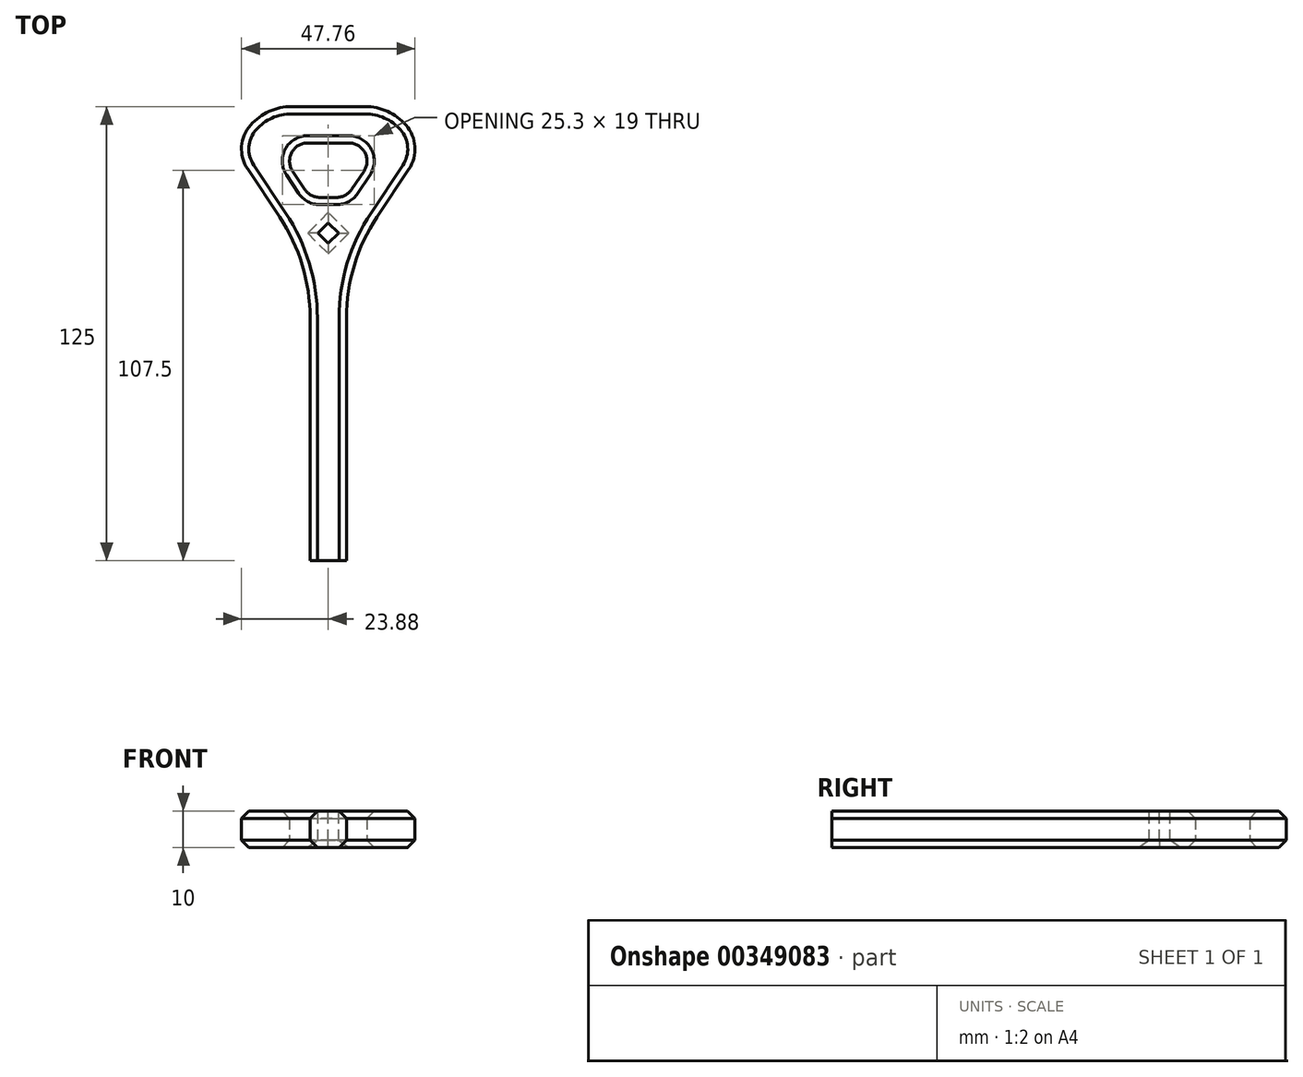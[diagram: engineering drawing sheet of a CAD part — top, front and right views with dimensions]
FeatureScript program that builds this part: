
annotation { "Feature Type Name" : "Feature", "Feature Type Description" : "" }
export const myFeature = defineFeature(function(context is Context, id is Id, definition is map)
    precondition{}
    {
        {
            var Q0;
            Q0=qCreatedBy(makeId("Top.planeOp"),FACE);
            var sketch = newSketch(context, id + "F0", { "sketchPlane" : qUnion([Q0])});
            skLineSegment(sketch, "E0.bottom", {"start": v(-5, 50) * mm, "end": v(5, 50) * mm});
            skLineSegment(sketch, "E0.top", {"start": v(-5, -50) * mm, "end": v(5, -50) * mm});
            skLineSegment(sketch, "E0.left", {"start": v(-5, 31.97) * mm, "end": v(-5, -50) * mm});
            skLineSegment(sketch, "E0.right", {"start": v(5, 31.97) * mm, "end": v(5, -50) * mm});
            skPoint(sketch, "E0.middle", {"position": v(0, 0) * mm});
            skLineSegment(sketch, "E1.bottom", {"start": v(-15, 75) * mm, "end": v(15, 75) * mm});
            skLineSegment(sketch, "E1.top", {"start": v(-15, 65) * mm, "end": v(15, 65) * mm});
            skLineSegment(sketch, "E1.left", {"start": v(-15, 75) * mm, "end": v(-15, 65) * mm});
            skLineSegment(sketch, "E1.right", {"start": v(15, 75) * mm, "end": v(15, 65) * mm});
            skPoint(sketch, "E1.middle", {"position": v(0, 70) * mm});
            skLineSegment(sketch, "E2", {"start": v(-15, 65) * mm, "end": v(-5, 50) * mm});
            skLineSegment(sketch, "E3", {"start": v(5, 50) * mm, "end": v(15, 65) * mm});
            skLineSegment(sketch, "E4", {"start": v(-5, 31.97) * mm, "end": v(-25, 61.97) * mm});
            skLineSegment(sketch, "E5", {"start": v(-25, 61.97) * mm, "end": v(-25, 75) * mm});
            skLineSegment(sketch, "E6", {"start": v(-25, 75) * mm, "end": v(-15, 75) * mm});
            skLineSegment(sketch, "E7.MirrorCS", {"start": v(5, 31.97) * mm, "end": v(25, 61.97) * mm});
            skLineSegment(sketch, "E8.MirrorCS", {"start": v(25, 75) * mm, "end": v(15, 75) * mm});
            skLineSegment(sketch, "E9.MirrorCS", {"start": v(25, 61.97) * mm, "end": v(25, 75) * mm});
            skSolve(sketch);
        }
        {
            var Q0;
            Q0=makeQuery(id+"F0.imprint","IMPRINT",FACE,{"disambiguationData":[TD([[makeQuery(id+"F0.imprint","IMPRINT",EDGE,{"derivedFrom":sQuery(id+"F0.wireOp",EDGE,"E0.bottom")}),-1.0]])]});
            var Q1;
            Q1=makeQuery(id+"F0.imprint","IMPRINT",FACE,{"disambiguationData":[TD([[makeQuery(id+"F0.imprint","IMPRINT",EDGE,{"derivedFrom":sQuery(id+"F0.wireOp",EDGE,"E1.bottom")}),-1.0]])]});
            extrude(context, id + "F1", {"entities" : qUnion([Q0, Q1]), "depth" : 10 * mm});
        }
        {
            var Q0;
            Q0=makeQuery(id+"F1.opExtrude","SWEPT_EDGE",EDGE,{"disambiguationData":[OSD([sQuery(id+"F0.wireOp",EDGE,"E1.top"),sQuery(id+"F0.wireOp",EDGE,"E1.right"),sQuery(id+"F0.wireOp",EDGE,"E3")])]});
            var Q1;
            Q1=makeQuery(id+"F1.opExtrude","SWEPT_EDGE",EDGE,{"disambiguationData":[OSD([sQuery(id+"F0.wireOp",EDGE,"E1.top"),sQuery(id+"F0.wireOp",EDGE,"E1.left"),sQuery(id+"F0.wireOp",EDGE,"E2")])]});
            var Q2;
            Q2=makeQuery(id+"F1.opExtrude","SWEPT_EDGE",EDGE,{"disambiguationData":[OSD([sQuery(id+"F0.wireOp",EDGE,"E0.bottom"),sQuery(id+"F0.wireOp",EDGE,"E2")])]});
            var Q3;
            Q3=makeQuery(id+"F1.opExtrude","SWEPT_EDGE",EDGE,{"disambiguationData":[OSD([sQuery(id+"F0.wireOp",EDGE,"E0.bottom"),sQuery(id+"F0.wireOp",EDGE,"E3")])]});
            fillet(context, id + "F2", {"entities" : qUnion([Q0, Q1, Q2, Q3]), "radius" : 5 * mm, "tangentPropagation" : true, "allowEdgeOverflow" : false});
        }
        {
            var Q0;
            Q0=makeQuery(id+"F1.opExtrude","SWEPT_EDGE",EDGE,{"disambiguationData":[OSD([sQuery(id+"F0.wireOp",EDGE,"E5"),sQuery(id+"F0.wireOp",EDGE,"E6")])]});
            var Q1;
            Q1=makeQuery(id+"F1.opExtrude","SWEPT_EDGE",EDGE,{"disambiguationData":[OSD([sQuery(id+"F0.wireOp",EDGE,"E8.MirrorCS"),sQuery(id+"F0.wireOp",EDGE,"E9.MirrorCS")])]});
            fillet(context, id + "F3", {"entities" : qUnion([Q0, Q1]), "radius" : 15 * mm, "tangentPropagation" : true, "allowEdgeOverflow" : false});
        }
        {
            var Q0;
            Q0=makeQuery(id+"F3.opFillet","BLEND_EDGE",EDGE,{"blendedFrom":[makeQuery(id+"F1.opExtrude","SWEPT_EDGE",EDGE,{"disambiguationData":[OSD([sQuery(id+"F0.wireOp",EDGE,"E5"),sQuery(id+"F0.wireOp",EDGE,"E6")])]}),makeQuery(id+"F1.opExtrude","SWEPT_FACE",FACE,{"disambiguationData":[OSD([sQuery(id+"F0.wireOp",EDGE,"E4")])]})],"blendedInto":[makeQuery(id+"F1.opExtrude","SWEPT_FACE",FACE,{"disambiguationData":[OSD([sQuery(id+"F0.wireOp",EDGE,"E4")])]})]});
            var Q1;
            Q1=makeQuery(id+"F3.opFillet","BLEND_EDGE",EDGE,{"blendedFrom":[makeQuery(id+"F1.opExtrude","SWEPT_EDGE",EDGE,{"disambiguationData":[OSD([sQuery(id+"F0.wireOp",EDGE,"E8.MirrorCS"),sQuery(id+"F0.wireOp",EDGE,"E9.MirrorCS")])]}),makeQuery(id+"F1.opExtrude","SWEPT_FACE",FACE,{"disambiguationData":[OSD([sQuery(id+"F0.wireOp",EDGE,"E7.MirrorCS")])]})],"blendedInto":[makeQuery(id+"F1.opExtrude","SWEPT_FACE",FACE,{"disambiguationData":[OSD([sQuery(id+"F0.wireOp",EDGE,"E7.MirrorCS")])]})]});
            fillet(context, id + "F4", {"entities" : qUnion([Q0, Q1]), "radius" : 10 * mm, "tangentPropagation" : true, "allowEdgeOverflow" : false});
        }
        {
            var Q0;
            Q0=makeQuery(id+"F1.opExtrude","SWEPT_EDGE",EDGE,{"disambiguationData":[OSD([sQuery(id+"F0.wireOp",EDGE,"E0.right"),sQuery(id+"F0.wireOp",EDGE,"E7.MirrorCS")])]});
            var Q1;
            Q1=makeQuery(id+"F1.opExtrude","SWEPT_EDGE",EDGE,{"disambiguationData":[OSD([sQuery(id+"F0.wireOp",EDGE,"E0.left"),sQuery(id+"F0.wireOp",EDGE,"E4")])]});
            fillet(context, id + "F5", {"entities" : qUnion([Q0, Q1]), "radius" : 50 * mm, "tangentPropagation" : true, "allowEdgeOverflow" : false});
        }
        {
            var Q0;
            Q0=makeQuery(id+"F1.opExtrude","CAP_EDGE",EDGE,{"disambiguationData":[OSD([sQuery(id+"F0.wireOp",EDGE,"E1.top")])],"isStart":false});
            var Q1;
            Q1=makeQuery(id+"F1.opExtrude","CAP_EDGE",EDGE,{"disambiguationData":[OSD([sQuery(id+"F0.wireOp",EDGE,"E1.bottom"),sQuery(id+"F0.wireOp",EDGE,"E6"),sQuery(id+"F0.wireOp",EDGE,"E8.MirrorCS")])],"isStart":false});
            var Q2;
            Q2=makeQuery(id+"F1.opExtrude","CAP_EDGE",EDGE,{"disambiguationData":[OSD([sQuery(id+"F0.wireOp",EDGE,"E0.bottom")])],"isStart":true});
            var Q3;
            Q3=makeQuery(id+"F1.opExtrude","CAP_EDGE",EDGE,{"disambiguationData":[OSD([sQuery(id+"F0.wireOp",EDGE,"E1.bottom"),sQuery(id+"F0.wireOp",EDGE,"E6"),sQuery(id+"F0.wireOp",EDGE,"E8.MirrorCS")])],"isStart":true});
            chamfer(context, id + "F6", {"entities" : qUnion([Q0, Q1, Q2, Q3]), "width" : 2 * mm, "tangentPropagation" : true});
        }
        {
            var Q0;
            Q0=makeQuery(id+"F1.opExtrude","CAP_FACE",FACE,{"disambiguationData":[OSD([sQuery(id+"F0.wireOp",EDGE,"E0.bottom"),sQuery(id+"F0.wireOp",EDGE,"E0.top"),sQuery(id+"F0.wireOp",EDGE,"E0.left"),sQuery(id+"F0.wireOp",EDGE,"E0.right"),sQuery(id+"F0.wireOp",EDGE,"E1.bottom"),sQuery(id+"F0.wireOp",EDGE,"E1.top"),sQuery(id+"F0.wireOp",EDGE,"E2"),sQuery(id+"F0.wireOp",EDGE,"E3"),sQuery(id+"F0.wireOp",EDGE,"E4"),sQuery(id+"F0.wireOp",EDGE,"E5"),sQuery(id+"F0.wireOp",EDGE,"E6"),sQuery(id+"F0.wireOp",EDGE,"E7.MirrorCS"),sQuery(id+"F0.wireOp",EDGE,"E8.MirrorCS"),sQuery(id+"F0.wireOp",EDGE,"E9.MirrorCS")])],"isStart":false});
            var sketch = newSketch(context, id + "F7", { "sketchPlane" : qUnion([Q0])});
            skLineSegment(sketch, "E10.bottom", {"start": v(2.83, 40.17) * mm, "end": v(0, 43) * mm});
            skLineSegment(sketch, "E10.top", {"start": v(0, 37.34) * mm, "end": v(-2.83, 40.17) * mm});
            skLineSegment(sketch, "E10.left", {"start": v(2.83, 40.17) * mm, "end": v(0, 37.34) * mm});
            skLineSegment(sketch, "E10.right", {"start": v(0, 43) * mm, "end": v(-2.83, 40.17) * mm});
            skPoint(sketch, "E10.middle", {"position": v(0, 40.17) * mm});
            skSolve(sketch);
        }
        {
            var Q0;
            Q0=makeQuery(id+"F7.imprint","IMPRINT",FACE,{"disambiguationData":[TD([[makeQuery(id+"F7.imprint","IMPRINT",EDGE,{"derivedFrom":sQuery(id+"F7.wireOp",EDGE,"E10.bottom")}),1.0]])]});
            extrude(context, id + "F8", {"entities" : qUnion([Q0]), "operationType" : NewBodyOperationType.REMOVE, "endBound" : BoundingType.THROUGH_ALL, "oppositeDirection" : true, "depth" : 25 * mm});
        }
        {
            var Q0;
            Q0=makeQuery(id+"F8.boolean.opBoolean","COPY",EDGE,{"derivedFrom":makeQuery(id+"F8.opExtrude","CAP_EDGE",EDGE,{"disambiguationData":[OSD([sQuery(id+"F7.wireOp",EDGE,"E10.bottom")])],"isStart":true})});
            var Q1;
            Q1=makeQuery(id+"F8.boolean.opBoolean","COPY",EDGE,{"derivedFrom":makeQuery(id+"F8.opExtrude","CAP_EDGE",EDGE,{"disambiguationData":[OSD([sQuery(id+"F7.wireOp",EDGE,"E10.right")])],"isStart":true})});
            var Q2;
            Q2=makeQuery(id+"F8.boolean.opBoolean","COPY",EDGE,{"derivedFrom":makeQuery(id+"F8.opExtrude","CAP_EDGE",EDGE,{"disambiguationData":[OSD([sQuery(id+"F7.wireOp",EDGE,"E10.left")])],"isStart":true})});
            var Q3;
            Q3=makeQuery(id+"F8.boolean.opBoolean","COPY",EDGE,{"derivedFrom":makeQuery(id+"F8.opExtrude","CAP_EDGE",EDGE,{"disambiguationData":[OSD([sQuery(id+"F7.wireOp",EDGE,"E10.top")])],"isStart":true})});
            var Q4;
            Q4=makeQuery(id+"F8.boolean.opBoolean","INTERSECT",EDGE,{"derivedFrom":[makeQuery(id+"F1.opExtrude","CAP_FACE",FACE,{"disambiguationData":[OSD([sQuery(id+"F0.wireOp",EDGE,"E0.bottom"),sQuery(id+"F0.wireOp",EDGE,"E0.top"),sQuery(id+"F0.wireOp",EDGE,"E0.left"),sQuery(id+"F0.wireOp",EDGE,"E0.right"),sQuery(id+"F0.wireOp",EDGE,"E1.bottom"),sQuery(id+"F0.wireOp",EDGE,"E1.top"),sQuery(id+"F0.wireOp",EDGE,"E2"),sQuery(id+"F0.wireOp",EDGE,"E3"),sQuery(id+"F0.wireOp",EDGE,"E4"),sQuery(id+"F0.wireOp",EDGE,"E5"),sQuery(id+"F0.wireOp",EDGE,"E6"),sQuery(id+"F0.wireOp",EDGE,"E7.MirrorCS"),sQuery(id+"F0.wireOp",EDGE,"E8.MirrorCS"),sQuery(id+"F0.wireOp",EDGE,"E9.MirrorCS")])],"isStart":true}),makeQuery(id+"F8.opExtrude","SWEPT_FACE",FACE,{"disambiguationData":[OSD([sQuery(id+"F7.wireOp",EDGE,"E10.left")])]})]});
            var Q5;
            Q5=makeQuery(id+"F8.boolean.opBoolean","INTERSECT",EDGE,{"derivedFrom":[makeQuery(id+"F1.opExtrude","CAP_FACE",FACE,{"disambiguationData":[OSD([sQuery(id+"F0.wireOp",EDGE,"E0.bottom"),sQuery(id+"F0.wireOp",EDGE,"E0.top"),sQuery(id+"F0.wireOp",EDGE,"E0.left"),sQuery(id+"F0.wireOp",EDGE,"E0.right"),sQuery(id+"F0.wireOp",EDGE,"E1.bottom"),sQuery(id+"F0.wireOp",EDGE,"E1.top"),sQuery(id+"F0.wireOp",EDGE,"E2"),sQuery(id+"F0.wireOp",EDGE,"E3"),sQuery(id+"F0.wireOp",EDGE,"E4"),sQuery(id+"F0.wireOp",EDGE,"E5"),sQuery(id+"F0.wireOp",EDGE,"E6"),sQuery(id+"F0.wireOp",EDGE,"E7.MirrorCS"),sQuery(id+"F0.wireOp",EDGE,"E8.MirrorCS"),sQuery(id+"F0.wireOp",EDGE,"E9.MirrorCS")])],"isStart":true}),makeQuery(id+"F8.opExtrude","SWEPT_FACE",FACE,{"disambiguationData":[OSD([sQuery(id+"F7.wireOp",EDGE,"E10.bottom")])]})]});
            var Q6;
            Q6=makeQuery(id+"F8.boolean.opBoolean","INTERSECT",EDGE,{"derivedFrom":[makeQuery(id+"F1.opExtrude","CAP_FACE",FACE,{"disambiguationData":[OSD([sQuery(id+"F0.wireOp",EDGE,"E0.bottom"),sQuery(id+"F0.wireOp",EDGE,"E0.top"),sQuery(id+"F0.wireOp",EDGE,"E0.left"),sQuery(id+"F0.wireOp",EDGE,"E0.right"),sQuery(id+"F0.wireOp",EDGE,"E1.bottom"),sQuery(id+"F0.wireOp",EDGE,"E1.top"),sQuery(id+"F0.wireOp",EDGE,"E2"),sQuery(id+"F0.wireOp",EDGE,"E3"),sQuery(id+"F0.wireOp",EDGE,"E4"),sQuery(id+"F0.wireOp",EDGE,"E5"),sQuery(id+"F0.wireOp",EDGE,"E6"),sQuery(id+"F0.wireOp",EDGE,"E7.MirrorCS"),sQuery(id+"F0.wireOp",EDGE,"E8.MirrorCS"),sQuery(id+"F0.wireOp",EDGE,"E9.MirrorCS")])],"isStart":true}),makeQuery(id+"F8.opExtrude","SWEPT_FACE",FACE,{"disambiguationData":[OSD([sQuery(id+"F7.wireOp",EDGE,"E10.right")])]})]});
            var Q7;
            Q7=makeQuery(id+"F8.boolean.opBoolean","INTERSECT",EDGE,{"derivedFrom":[makeQuery(id+"F1.opExtrude","CAP_FACE",FACE,{"disambiguationData":[OSD([sQuery(id+"F0.wireOp",EDGE,"E0.bottom"),sQuery(id+"F0.wireOp",EDGE,"E0.top"),sQuery(id+"F0.wireOp",EDGE,"E0.left"),sQuery(id+"F0.wireOp",EDGE,"E0.right"),sQuery(id+"F0.wireOp",EDGE,"E1.bottom"),sQuery(id+"F0.wireOp",EDGE,"E1.top"),sQuery(id+"F0.wireOp",EDGE,"E2"),sQuery(id+"F0.wireOp",EDGE,"E3"),sQuery(id+"F0.wireOp",EDGE,"E4"),sQuery(id+"F0.wireOp",EDGE,"E5"),sQuery(id+"F0.wireOp",EDGE,"E6"),sQuery(id+"F0.wireOp",EDGE,"E7.MirrorCS"),sQuery(id+"F0.wireOp",EDGE,"E8.MirrorCS"),sQuery(id+"F0.wireOp",EDGE,"E9.MirrorCS")])],"isStart":true}),makeQuery(id+"F8.opExtrude","SWEPT_FACE",FACE,{"disambiguationData":[OSD([sQuery(id+"F7.wireOp",EDGE,"E10.top")])]})]});
            chamfer(context, id + "F9", {"entities" : qUnion([Q0, Q1, Q2, Q3, Q4, Q5, Q6, Q7]), "width" : 2 * mm, "tangentPropagation" : true});
        }
    });
